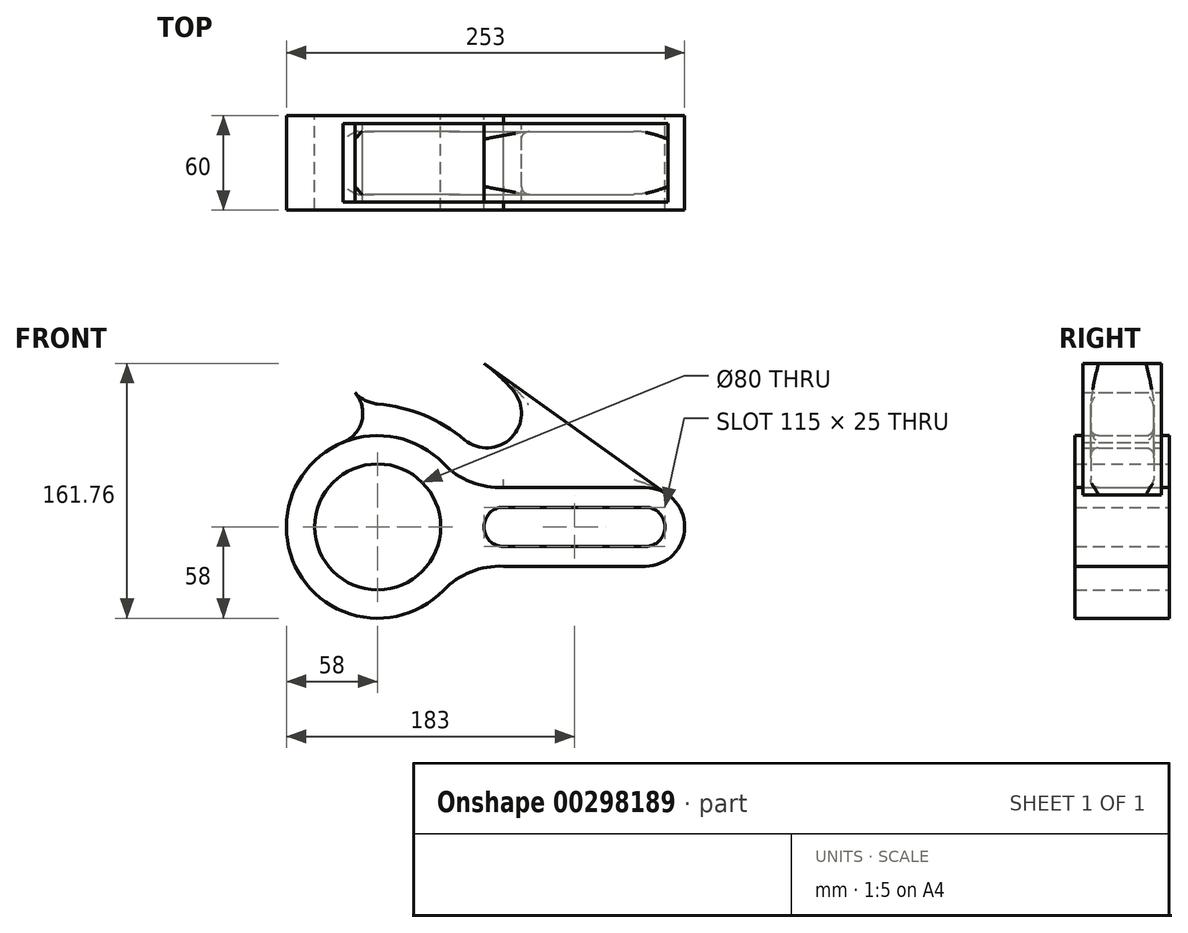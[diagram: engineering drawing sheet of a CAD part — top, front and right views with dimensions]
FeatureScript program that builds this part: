
annotation { "Feature Type Name" : "Feature", "Feature Type Description" : "" }
export const myFeature = defineFeature(function(context is Context, id is Id, definition is map)
    precondition{}
    {
        {
            var Q0;
            Q0=qCreatedBy(makeId("Front.planeOp"),FACE);
            var sketch = newSketch(context, id + "F0", { "sketchPlane" : qUnion([Q0])});
            skCircle(sketch, "E0", {"center": v(0, 0) * mm, "radius": 40 * mm});
            skSolve(sketch);
        }
        {
            var Q0;
            Q0=qCreatedBy(makeId("Front.planeOp"),FACE);
            var sketch = newSketch(context, id + "F1", { "sketchPlane" : qUnion([Q0])});
            skLineSegment(sketch, "E1", {"start": v(80, -25) * mm, "end": v(170, -25) * mm});
            skLineSegment(sketch, "E2", {"start": v(80, 25) * mm, "end": v(170, 25) * mm});
            skPoint(sketch, "E3.endSnap0", {"position": v(-58, 0) * mm});
            skArc(sketch, "E4", {"start": v(170, -25) * mm, "mid": v(195, 0) * mm, "end": v(170, 25) * mm});
            skLineSegment(sketch, "E5", {"start": v(80, 12.5) * mm, "end": v(170, 12.5) * mm});
            skLineSegment(sketch, "E6", {"start": v(80, -12.5) * mm, "end": v(170, -12.5) * mm});
            skArc(sketch, "E7", {"start": v(170, -12.5) * mm, "mid": v(182.5, 0) * mm, "end": v(170, 12.5) * mm});
            skArc(sketch, "E8", {"start": v(80, 12.5) * mm, "mid": v(67.5, 0) * mm, "end": v(80, -12.5) * mm});
            skArc(sketch, "E9", {"start": v(41.76, 40.25) * mm, "mid": v(-58, 0) * mm, "end": v(41.76, -40.25) * mm});
            skArc(sketch, "E10", {"start": v(41.76, -40.25) * mm, "mid": v(59.24, -28.5) * mm, "end": v(80, -25) * mm});
            skArc(sketch, "E11", {"start": v(41.76, 40.25) * mm, "mid": v(59.24, 28.5) * mm, "end": v(80, 25) * mm});
            skLineSegment(sketch, "E12", {"start": v(125, 25) * mm, "end": v(125, -25) * mm, "construction": true});
            skArc(sketch, "E13", {"start": v(-21.9, 53.7) * mm, "mid": v(-9.98, 67.65) * mm, "end": v(-14.44, 85.44) * mm});
            skLineSegment(sketch, "E14", {"start": v(0, -71.53) * mm, "end": v(0, 188.98) * mm, "construction": true});
            skLineSegment(sketch, "E15", {"start": v(0, 0) * mm, "end": v(138.53, 138.53) * mm, "construction": true});
            skLineSegment(sketch, "E16", {"start": v(47.66, 0) * mm, "end": v(216.94, 0) * mm, "construction": true});
            skPoint(sketch, "E16.endSnap0", {"position": v(195, 0) * mm});
            skArc(sketch, "E17", {"start": v(0, 121.88) * mm, "mid": v(-19.92, 99.98) * mm, "end": v(0, 78.08) * mm});
            skArc(sketch, "E18", {"start": v(85.55, 51.77) * mm, "mid": v(38.83, 92.15) * mm, "end": v(-22.7, 97.4) * mm, "construction": true});
            skArc(sketch, "E19", {"start": v(0, 121.88) * mm, "mid": v(47.56, 114.78) * mm, "end": v(86.3, 86.3) * mm});
            skArc(sketch, "E20", {"start": v(0, 78.08) * mm, "mid": v(29.4, 70.93) * mm, "end": v(55.31, 55.31) * mm});
            skArc(sketch, "E21", {"start": v(55.31, 55.31) * mm, "mid": v(84.94, 56.67) * mm, "end": v(86.3, 86.3) * mm});
            skArc(sketch, "E22", {"start": v(0, 108.74) * mm, "mid": v(-6.92, 99.98) * mm, "end": v(0, 91.22) * mm});
            skArc(sketch, "E23", {"start": v(64.6, 64.6) * mm, "mid": v(75.75, 65.86) * mm, "end": v(77, 77) * mm});
            skArc(sketch, "E24", {"start": v(64.6, 64.6) * mm, "mid": v(34.7, 83.74) * mm, "end": v(0, 91.22) * mm});
            skArc(sketch, "E25", {"start": v(77, 77) * mm, "mid": v(41.96, 101.27) * mm, "end": v(0, 108.74) * mm});
            skLineSegment(sketch, "E26", {"start": v(67.47, 103.76) * mm, "end": v(184.5, 20.36) * mm});
            skSolve(sketch);
        }
        {
            var Q0;
            Q0=makeQuery(id+"F1.imprint","IMPRINT",FACE,{"disambiguationData":[TD([[makeQuery(id+"F1.imprint","IMPRINT",EDGE,{"derivedFrom":sQuery(id+"F1.wireOp",EDGE,"E1")}),1.0]])]});
            extrude(context, id + "F2", {"entities" : qUnion([Q0]), "depth" : 60 * mm});
        }
        {
            var Q0;
            Q0 = qSketchRegion(id + "F0", true);
            extrude(context, id + "F3", {"entities" : qUnion([Q0]), "operationType" : NewBodyOperationType.REMOVE, "endBound" : BoundingType.THROUGH_ALL, "depth" : 25 * mm});
        }
        {
            var Q0;
            {var subQ1=sQuery(id+"F1.wireOp",EDGE,"E19");Q0=makeQuery(id+"F1.imprint","IMPRINT",FACE,{"disambiguationData":[TD([[makeQuery(id+"F1.imprint","IMPRINT",EDGE,{"derivedFrom":subQ1}),-1.0]])]});}
            extrude(context, id + "F4", {"entities" : qUnion([Q0]), "depth" : 55 * mm, "hasSecondDirection" : true, "secondDirectionOppositeDirection" : false, "secondDirectionDepth" : 5 * mm});
        }
        {
            var Q0;
            {var subQ4=sQuery(id+"F1.wireOp",EDGE,"E2");Q0=makeQuery(id+"F1.imprint","IMPRINT",FACE,{"disambiguationData":[TD([[makeQuery(id+"F1.imprint","IMPRINT",EDGE,{"derivedFrom":subQ4}),1.0]])]});}
            extrude(context, id + "F5", {"entities" : qUnion([Q0]), "depth" : 50 * mm, "hasSecondDirection" : true, "secondDirectionOppositeDirection" : false, "secondDirectionDepth" : 10 * mm});
        }
        {
            var Q0;
            Q0=makeQuery(id+"F5.opExtrude","CAP_EDGE",EDGE,{"disambiguationData":[OSD([sQuery(id+"F1.wireOp",EDGE,"E4")])],"isStart":true});
            var Q1;
            Q1=makeQuery(id+"F5.opExtrude","CAP_EDGE",EDGE,{"disambiguationData":[OSD([sQuery(id+"F1.wireOp",EDGE,"E2")])],"isStart":true});
            var Q2;
            Q2=makeQuery(id+"F5.opExtrude","CAP_EDGE",EDGE,{"disambiguationData":[OSD([sQuery(id+"F1.wireOp",EDGE,"E11")])],"isStart":true});
            var Q3;
            Q3=makeQuery(id+"F5.opExtrude","CAP_EDGE",EDGE,{"disambiguationData":[OSD([sQuery(id+"F1.wireOp",EDGE,"E9")])],"isStart":true});
            var Q4;
            Q4=makeQuery(id+"F5.opExtrude","CAP_EDGE",EDGE,{"disambiguationData":[OSD([sQuery(id+"F1.wireOp",EDGE,"E19")])],"isStart":true});
            var Q5;
            Q5=makeQuery(id+"F5.opExtrude","CAP_EDGE",EDGE,{"disambiguationData":[OSD([sQuery(id+"F1.wireOp",EDGE,"E17")])],"isStart":true});
            var Q6;
            Q6=makeQuery(id+"F5.opExtrude","CAP_EDGE",EDGE,{"disambiguationData":[OSD([sQuery(id+"F1.wireOp",EDGE,"E20")])],"isStart":true});
            var Q7;
            Q7=makeQuery(id+"F5.opExtrude","CAP_EDGE",EDGE,{"disambiguationData":[OSD([sQuery(id+"F1.wireOp",EDGE,"E26")])],"isStart":true});
            fillet(context, id + "F6", {"entities" : qUnion([Q0, Q1, Q2, Q3, Q4, Q5, Q6, Q7]), "radius" : 5 * mm, "tangentPropagation" : true, "allowEdgeOverflow" : false});
        }
        {
            var Q0;
            Q0=makeQuery(id+"F5.opExtrude","CAP_EDGE",EDGE,{"disambiguationData":[OSD([sQuery(id+"F1.wireOp",EDGE,"E26")])],"isStart":false});
            var Q1;
            Q1=makeQuery(id+"F5.opExtrude","CAP_EDGE",EDGE,{"disambiguationData":[OSD([sQuery(id+"F1.wireOp",EDGE,"E21")])],"isStart":false});
            var Q2;
            Q2=makeQuery(id+"F5.opExtrude","CAP_EDGE",EDGE,{"disambiguationData":[OSD([sQuery(id+"F1.wireOp",EDGE,"E19")])],"isStart":false});
            var Q3;
            Q3=makeQuery(id+"F5.opExtrude","CAP_EDGE",EDGE,{"disambiguationData":[OSD([sQuery(id+"F1.wireOp",EDGE,"E4")])],"isStart":false});
            var Q4;
            Q4=makeQuery(id+"F5.opExtrude","CAP_EDGE",EDGE,{"disambiguationData":[OSD([sQuery(id+"F1.wireOp",EDGE,"E2")])],"isStart":false});
            var Q5;
            Q5=makeQuery(id+"F5.opExtrude","CAP_EDGE",EDGE,{"disambiguationData":[OSD([sQuery(id+"F1.wireOp",EDGE,"E11")])],"isStart":false});
            var Q6;
            Q6=makeQuery(id+"F5.opExtrude","CAP_EDGE",EDGE,{"disambiguationData":[OSD([sQuery(id+"F1.wireOp",EDGE,"E9")])],"isStart":false});
            fillet(context, id + "F7", {"entities" : qUnion([Q0, Q1, Q2, Q3, Q4, Q5, Q6]), "radius" : 5 * mm, "tangentPropagation" : true, "allowEdgeOverflow" : false});
        }
    });
